FCSTD DOCUMENT  (FreeCAD 0.19R24291 (Git))
Label: mini-pc
License: All rights reserved
LicenseURL: http://en.wikipedia.org/wiki/All_rights_reserved
objects: Sketcher::SketchObject×1, PartDesign::Body×1
note: 2 computed .brp shape members not serialized (recipe doc carries the construction recipe); baked Part::Feature solids carry a one-line shape summary decoded from their .brp

FEATURE [Sketcher::SketchObject] Sketch
  FullyConstrained = true
  MapMode = 5
  Support = -> [XY_Plane]
  sketch-geometry (54):
    g0: LineSegment StartX=-82 StartY=42 StartZ=0 EndX=82 EndY=42 EndZ=0
    g1: LineSegment StartX=82 StartY=42 StartZ=0 EndX=82 EndY=-42 EndZ=0
    g2: LineSegment StartX=82 StartY=-42 StartZ=0 EndX=-82 EndY=-42 EndZ=0
    g3: LineSegment StartX=-82 StartY=-42 StartZ=0 EndX=-82 EndY=42 EndZ=0
    g4: Circle CenterX=-72 CenterY=39 CenterZ=0 NormalX=0 NormalY=0 NormalZ=1 AngleXU=0 Radius=1
    g5: Circle CenterX=-4 CenterY=39 CenterZ=0 NormalX=0 NormalY=0 NormalZ=1 AngleXU=0 Radius=1
    g6: Circle CenterX=62.8 CenterY=39 CenterZ=0 NormalX=0 NormalY=0 NormalZ=1 AngleXU=0 Radius=1
    g7: Circle CenterX=-72 CenterY=-36 CenterZ=0 NormalX=0 NormalY=0 NormalZ=1 AngleXU=0 Radius=1
    g8: Circle CenterX=-33 CenterY=-39 CenterZ=0 NormalX=0 NormalY=0 NormalZ=1 AngleXU=0 Radius=1
    g9: Circle CenterX=22.8 CenterY=-39 CenterZ=0 NormalX=0 NormalY=0 NormalZ=1 AngleXU=0 Radius=1
    g10: Circle CenterX=-11 CenterY=32 CenterZ=0 NormalX=0 NormalY=0 NormalZ=1 AngleXU=0 Radius=1
    g11: Circle CenterX=29 CenterY=32 CenterZ=0 NormalX=0 NormalY=0 NormalZ=1 AngleXU=0 Radius=1
    g12: Circle CenterX=-11 CenterY=-8 CenterZ=0 NormalX=0 NormalY=0 NormalZ=1 AngleXU=0 Radius=1
    g13: Circle CenterX=29 CenterY=-8 CenterZ=0 NormalX=0 NormalY=0 NormalZ=1 AngleXU=0 Radius=1
    g14: Circle CenterX=-38.3 CenterY=30.86 CenterZ=0 NormalX=0 NormalY=0 NormalZ=1 AngleXU=0 Radius=1.5
    g15: Circle CenterX=-38.3 CenterY=-30.86 CenterZ=0 NormalX=0 NormalY=0 NormalZ=1 AngleXU=0 Radius=1.5
    g16: Circle CenterX=38.3 CenterY=30.86 CenterZ=0 NormalX=0 NormalY=0 NormalZ=1 AngleXU=0 Radius=1.5
    g17: Circle CenterX=38.3 CenterY=-30.86 CenterZ=0 NormalX=0 NormalY=0 NormalZ=1 AngleXU=0 Radius=1.5
    g18: LineSegment StartX=-7 StartY=32 StartZ=0 EndX=-5 EndY=32 EndZ=0
    g19: LineSegment StartX=-5 StartY=32 StartZ=0 EndX=-5 EndY=-8 EndZ=0
    g20: LineSegment StartX=-5 StartY=-8 StartZ=0 EndX=-7 EndY=-8 EndZ=0
    g21: LineSegment StartX=-7 StartY=-8 StartZ=0 EndX=-7 EndY=32 EndZ=0
    g22: LineSegment StartX=-1 StartY=32 StartZ=0 EndX=1 EndY=32 EndZ=0
    g23: LineSegment StartX=1 StartY=32 StartZ=0 EndX=1 EndY=-8 EndZ=0
    g24: LineSegment StartX=1 StartY=-8 StartZ=0 EndX=-1 EndY=-8 EndZ=0
    g25: LineSegment StartX=-1 StartY=-8 StartZ=0 EndX=-1 EndY=32 EndZ=0
    g26: LineSegment StartX=5 StartY=32 StartZ=0 EndX=7 EndY=32 EndZ=0
    g27: LineSegment StartX=7 StartY=32 StartZ=0 EndX=7 EndY=-8 EndZ=0
    g28: LineSegment StartX=7 StartY=-8 StartZ=0 EndX=5 EndY=-8 EndZ=0
    g29: LineSegment StartX=5 StartY=-8 StartZ=0 EndX=5 EndY=32 EndZ=0
    g30: LineSegment StartX=11 StartY=32 StartZ=0 EndX=13 EndY=32 EndZ=0
    g31: LineSegment StartX=13 StartY=32 StartZ=0 EndX=13 EndY=-8 EndZ=0
    g32: LineSegment StartX=13 StartY=-8 StartZ=0 EndX=11 EndY=-8 EndZ=0
    g33: LineSegment StartX=11 StartY=-8 StartZ=0 EndX=11 EndY=32 EndZ=0
    g34: LineSegment StartX=17 StartY=32 StartZ=0 EndX=19 EndY=32 EndZ=0
    g35: LineSegment StartX=19 StartY=32 StartZ=0 EndX=19 EndY=-8 EndZ=0
    g36: LineSegment StartX=19 StartY=-8 StartZ=0 EndX=17 EndY=-8 EndZ=0
    g37: LineSegment StartX=17 StartY=-8 StartZ=0 EndX=17 EndY=32 EndZ=0
    g38: LineSegment StartX=23 StartY=32 StartZ=0 EndX=25 EndY=32 EndZ=0
    g39: LineSegment StartX=25 StartY=32 StartZ=0 EndX=25 EndY=-8 EndZ=0
    g40: LineSegment StartX=25 StartY=-8 StartZ=0 EndX=23 EndY=-8 EndZ=0
    g41: LineSegment StartX=23 StartY=-8 StartZ=0 EndX=23 EndY=32 EndZ=0
    g42: Circle CenterX=-28.3 CenterY=30.86 CenterZ=0 NormalX=0 NormalY=0 NormalZ=1 AngleXU=0 Radius=1.5
    g43: Circle CenterX=48.3 CenterY=30.86 CenterZ=0 NormalX=0 NormalY=0 NormalZ=1 AngleXU=0 Radius=1.5
    g44: Circle CenterX=-28.3 CenterY=-30.86 CenterZ=0 NormalX=0 NormalY=0 NormalZ=1 AngleXU=0 Radius=1.5
    g45: Circle CenterX=48.3 CenterY=-30.86 CenterZ=0 NormalX=0 NormalY=0 NormalZ=1 AngleXU=0 Radius=1.5
    g46: LineSegment StartX=29 StartY=29 StartZ=0 EndX=31 EndY=29 EndZ=0
    g47: LineSegment StartX=31 StartY=29 StartZ=0 EndX=31 EndY=-5 EndZ=0
    g48: LineSegment StartX=31 StartY=-5 StartZ=0 EndX=29 EndY=-5 EndZ=0
    g49: LineSegment StartX=29 StartY=-5 StartZ=0 EndX=29 EndY=29 EndZ=0
    g50: LineSegment StartX=-13 StartY=29 StartZ=0 EndX=-11 EndY=29 EndZ=0
    g51: LineSegment StartX=-11 StartY=29 StartZ=0 EndX=-11 EndY=-5 EndZ=0
    g52: LineSegment StartX=-11 StartY=-5 StartZ=0 EndX=-13 EndY=-5 EndZ=0
    g53: LineSegment StartX=-13 StartY=-5 StartZ=0 EndX=-13 EndY=29 EndZ=0
  constraints (157):
    c: Coincident(g0,g1)
    c: Coincident(g1,g2)
    c: Coincident(g2,g3)
    c: Coincident(g3,g0)
    c: Horizontal(g2)
    c: Vertical(g1)
    c: Symmetric(g0,g0,g-2)
    c: Symmetric(g0,g2,g-1)
    c: DistanceX(g0,g0) = 164
    c: DistanceY(g3,g3) = 84
    c: DistanceY(g4,g0) = 3
    c: DistanceX(g0,g4) = 10
    c: Radius(g4) = 1
    c: Horizontal(g4,g5)
    c: Horizontal(g5,g6)
    c: DistanceX(g4,g5) = 68
    c: DistanceX(g5,g6) = 66.8
    c: Radius(g5) = 1
    c: Radius(g6) = 1
    c: Vertical(g7,g4)
    c: DistanceY(g2,g7) = 6
    c: DistanceX(g2,g8) = 49
    c: DistanceY(g2,g8) = 3
    c: Horizontal(g8,g9)
    c: DistanceX(g8,g9) = 55.8
    c: Radius(g8) = 1
    c: Radius(g9) = 1
    c: Radius(g7) = 1
    c: DistanceY(g10,g5) = 7
    c: Horizontal(g10,g11)
    c: DistanceX(g10,g11) = 40
    c: Vertical(g10,g12)
    c: DistanceY(g12,g10) = 40
    c: Vertical(g11,g13)
    c: DistanceY(g13,g11) = 40
    c: Radius(g10) = 1
    c: Radius(g11) = 1
    c: Radius(g12) = 1
    c: Radius(g13) = 1
    c: Symmetric(g14,g16,g-2)
    c: Symmetric(g14,g15,g-1)
    c: Symmetric(g16,g17,g-1)
    c: DistanceX(g14,g16) = 76.6
    c: DistanceY(g15,g14) = 61.72
    c: Radius(g14) = 1.5
    c: Radius(g16) = 1.5
    c: Radius(g15) = 1.5
    c: Radius(g17) = 1.5
    c: DistanceX(g10,g5) = 7
    c: Coincident(g18,g19)
    c: Coincident(g19,g20)
    c: Coincident(g20,g21)
    c: Coincident(g21,g18)
    c: Horizontal(g18)
    c: Horizontal(g20)
    c: Vertical(g19)
    c: Vertical(g21)
    c: Coincident(g22,g23)
    c: Coincident(g23,g24)
    c: Coincident(g24,g25)
    c: Coincident(g25,g22)
    c: Horizontal(g22)
    c: Horizontal(g24)
    c: Vertical(g23)
    c: Vertical(g25)
    c: Coincident(g26,g27)
    c: Coincident(g27,g28)
    c: Coincident(g28,g29)
    c: Coincident(g29,g26)
    c: Horizontal(g26)
    c: Horizontal(g28)
    c: Vertical(g27)
    c: Vertical(g29)
    c: Coincident(g30,g31)
    c: Coincident(g31,g32)
    c: Coincident(g32,g33)
    c: Coincident(g33,g30)
    c: Horizontal(g30)
    c: Horizontal(g32)
    c: Vertical(g31)
    c: Vertical(g33)
    c: Coincident(g34,g35)
    c: Coincident(g35,g36)
    c: Coincident(g36,g37)
    c: Coincident(g37,g34)
    c: Horizontal(g34)
    c: Horizontal(g36)
    c: Vertical(g35)
    c: Vertical(g37)
    c: Coincident(g38,g39)
    c: Coincident(g39,g40)
    c: Coincident(g40,g41)
    c: Coincident(g41,g38)
    c: Horizontal(g38)
    c: Horizontal(g40)
    c: Vertical(g39)
    c: Vertical(g41)
    c: Horizontal(g12,g20)
    c: Horizontal(g10,g18)
    c: DistanceX(g10,g18) = 4
    c: DistanceX(g18,g18) = 2
    c: Horizontal(g19,g24)
    c: Horizontal(g18,g22)
    c: DistanceX(g18,g22) = 4
    c: DistanceX(g22,g22) = 2
    c: Horizontal(g22,g26)
    c: Horizontal(g23,g28)
    c: DistanceX(g23,g28) = 4
    c: DistanceX(g28,g27) = 2
    c: DistanceX(g27,g32) = 4
    c: Horizontal(g27,g32)
    c: Horizontal(g26,g30)
    c: DistanceX(g32,g31) = 2
    c: DistanceX(g31,g36) = 4
    c: Horizontal(g30,g34)
    c: DistanceX(g34,g34) = 2
    c: Horizontal(g31,g36)
    c: Horizontal(g35,g40)
    c: DistanceX(g35,g40) = 4
    c: Horizontal(g34,g38)
    c: DistanceX(g38,g38) = 2
    c: Horizontal(g14,g42)
    c: DistanceX(g14,g42) = 10
    c: Horizontal(g15,g44)
    c: DistanceX(g15,g44) = 10
    c: Horizontal(g17,g45)
    c: DistanceX(g17,g45) = 10
    c: Horizontal(g16,g43)
    c: DistanceX(g16,g43) = 10
    c: Radius(g42) = 1.5
    c: Radius(g44) = 1.5
    c: Radius(g43) = 1.5
    c: Radius(g45) = 1.5
    c: Coincident(g46,g47)
    c: Coincident(g47,g48)
    c: Coincident(g48,g49)
    c: Coincident(g49,g46)
    c: Horizontal(g46)
    c: Horizontal(g48)
    c: Vertical(g47)
    c: Vertical(g49)
    c: Equal(g38,g46) = 2
    c: DistanceX(g39,g48) = 4
    c: DistanceY(g48,g46) = 34
    c: DistanceY(g46,g11) = 3
    c: Coincident(g50,g51)
    c: Coincident(g51,g52)
    c: Coincident(g52,g53)
    c: Coincident(g53,g50)
    c: Horizontal(g50)
    c: Horizontal(g52)
    c: Vertical(g51)
    c: Vertical(g53)
    c: DistanceY(g52,g50) = 34
    c: Vertical(g50,g10)
    c: DistanceY(g50,g10) = 3
    c: DistanceX(g50,g50) = 2
FEATURE [PartDesign::Body] Body
  Group = -> [Sketch]
  Origin = -> Origin
